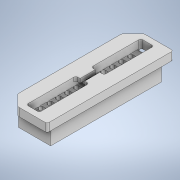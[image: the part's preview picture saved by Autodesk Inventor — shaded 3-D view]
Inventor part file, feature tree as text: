
AUTODESK INVENTOR PART (.ipt)
format: ipt  version: 2021 (Build 250183000, 183)  size: 391,168 bytes
history: native  units: mm
features: extrude x5, sketch x5, fillet x3, plane x2, chamfer x1
ambient origin geometry x8: Origin, YZ Plane, XZ Plane, XY Plane, X Axis, Y Axis, Z Axis, Center Point
bodies: Solid1 (feature_tree)
feature tree (16):
  plane  "Work Plane1"
  plane  "Work Plane2"
  extrude  "Extrusion1"  Depth=40.0mm
  extrude  "Extrusion2"  Depth=113.5mm
  extrude  "Extrusion5"  Depth=4.0mm TaperAngle=0.0deg
  extrude  "Extrusion6"  Depth=110.0mm
  fillet  "Fillet4"  Radius=17.0mm
  extrude  "Extrusion3"  Depth=10.0mm
  fillet  "Fillet3"  Radius=15.0mm
  chamfer  "Chamfer1"  Distance=4.25mm
  fillet  "Fillet5"  Radius=4.25mm
  sketch  "Sketch1"  dims[d0=40.0mm d1=125.0mm]
  sketch  "Sketch2"  dims[d2=13.0mm d3=113.5mm]
  sketch  "Sketch4"  dims[d5=13.5mm d6=4.0mm d7=0.0mm]
  sketch  "Sketch11"  dims[d8=32.0mm d9=110.0mm d12=17.0mm d13=0.0mm]
  sketch  "Sketch15"  dims[d14=4.0mm d15=7.5mm d16=15.0mm d17=4.25mm d18=4.25mm d20=4.0mm d21=0.0mm d32=25.0mm d33=60.0mm d53=4.0mm d54=4.0mm d56=13.0mm d57=0.0mm d58=5.75mm d61=4.0mm d63=4.0mm d67=4.9mm d69=13.0mm d72=100.0mm d74=8.9mm d75=10.0mm d77=10.0mm d79=4.0mm d80=0.0mm d82=55.0mm d85=2.0mm d86=2.0mm d87=11.0mm d88=2.0mm d89=45.0deg d90=3.0mm d91=0.0mm d92=0.0mm d94=0.0mm d95=4.0mm d96=20.0mm d98=9.0mm d99=10.0mm d101=10.0mm d68=0.872665mm d70=0.872665mm]
